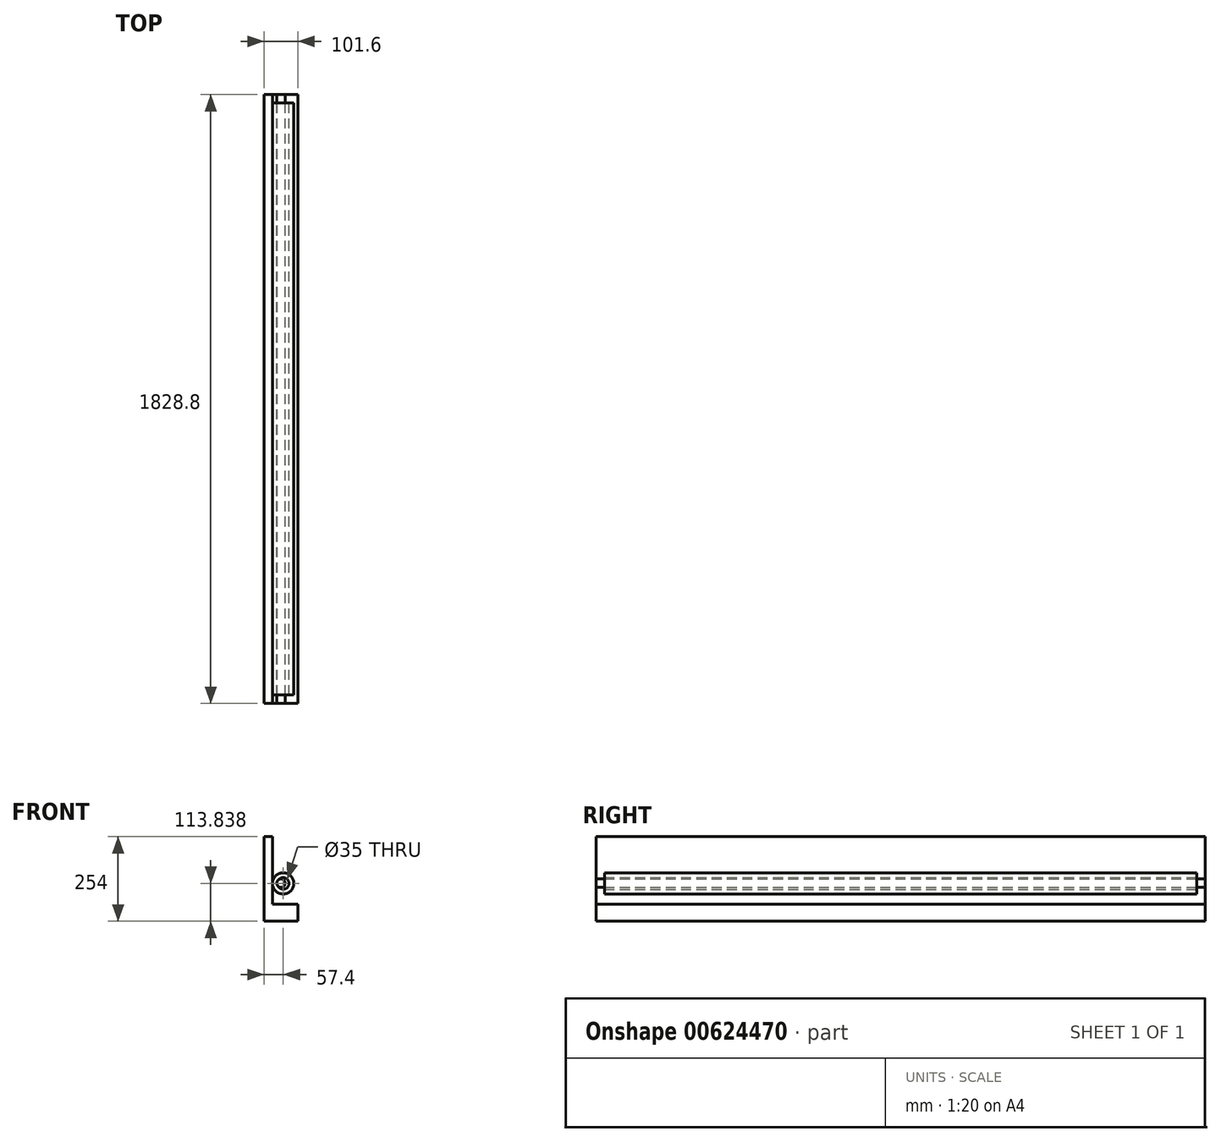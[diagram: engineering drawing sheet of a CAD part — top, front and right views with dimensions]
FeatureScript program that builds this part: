
annotation { "Feature Type Name" : "Feature", "Feature Type Description" : "" }
export const myFeature = defineFeature(function(context is Context, id is Id, definition is map)
    precondition{}
    {
        {
            var Q0;
            Q0=qCreatedBy(makeId("Front.planeOp"),FACE);
            var sketch = newSketch(context, id + "F0", { "sketchPlane" : qUnion([Q0])});
            skLineSegment(sketch, "E0", {"start": v(0, 0) * mm, "end": v(0, 203.2) * mm});
            skLineSegment(sketch, "E1", {"start": v(0, 203.2) * mm, "end": v(-25.4, 203.2) * mm});
            skLineSegment(sketch, "E2", {"start": v(-25.4, 203.2) * mm, "end": v(-25.4, -50.8) * mm});
            skLineSegment(sketch, "E3", {"start": v(-25.4, -50.8) * mm, "end": v(76.2, -50.8) * mm});
            skLineSegment(sketch, "E4", {"start": v(76.2, -50.8) * mm, "end": v(76.2, 0) * mm});
            skLineSegment(sketch, "E5", {"start": v(76.2, 0) * mm, "end": v(0, 0) * mm});
            skCircle(sketch, "E6", {"center": v(25.4, 63.5) * mm, "radius": 12.7 * mm});
            skSolve(sketch);
        }
        {
            var Q0;
            Q0=makeQuery(id+"F0.imprint","IMPRINT",FACE,{"disambiguationData":[TD([[makeQuery(id+"F0.imprint","IMPRINT",EDGE,{"derivedFrom":sQuery(id+"F0.wireOp",EDGE,"E0")}),1.0]])]});
            var Q1;
            Q1=makeQuery(id+"F0.imprint","IMPRINT",FACE,{"disambiguationData":[TD([[makeQuery(id+"F0.imprint","IMPRINT",EDGE,{"derivedFrom":sQuery(id+"F0.wireOp",EDGE,"E6")}),1.0]])]});
            extrude(context, id + "F1", {"entities" : qUnion([Q0, Q1]), "endBound" : BoundingType.SYMMETRIC, "depth" : 1828.8 * mm, "offsetDistance" : 25.4 * mm});
        }
        {
            var Q0;
            Q0=qCreatedBy(makeId("Front.planeOp"),FACE);
            var sketch = newSketch(context, id + "F2", { "sketchPlane" : qUnion([Q0])});
            skCircle(sketch, "E7", {"center": v(32, 63.04) * mm, "radius": 17.5 * mm});
            skCircle(sketch, "E8", {"center": v(32, 63.04) * mm, "radius": 32 * mm});
            skSolve(sketch);
        }
        {
            var Q0;
            Q0=makeQuery(id+"F2.imprint","IMPRINT",FACE,{"disambiguationData":[TD([[makeQuery(id+"F2.imprint","IMPRINT",EDGE,{"derivedFrom":sQuery(id+"F2.wireOp",EDGE,"E7")}),-1.0]])]});
            extrude(context, id + "F3", {"entities" : qUnion([Q0]), "endBound" : BoundingType.SYMMETRIC, "depth" : 1778 * mm, "offsetDistance" : 25.4 * mm});
        }
    });
